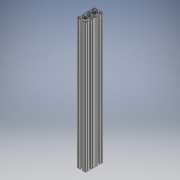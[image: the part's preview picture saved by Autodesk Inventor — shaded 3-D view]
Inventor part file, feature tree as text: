
AUTODESK INVENTOR PART (.ipt)
format: ipt  version: 2018 (Build 220112000, 112)  size: 629,248 bytes
history: native  units: mm
features: other x1, extrude x1, sketch x1
ambient origin geometry x8: Origin, YZ Plane, XZ Plane, XY Plane, X Axis, Y Axis, Z Axis, Center Point
bodies: Body1 (feature_tree)
feature tree (3):
  other  "Sólido1"
  extrude  "Extrusão1"  [1 undecoded]
  sketch  "Esboço1"  dims[d0=585.0mm d1=0.0mm]
note: 1 required parameter value undecoded (feature->parameter linkage not recoverable at this tier; creation-order binding heuristic only, values carry confidence <= 0.55)
